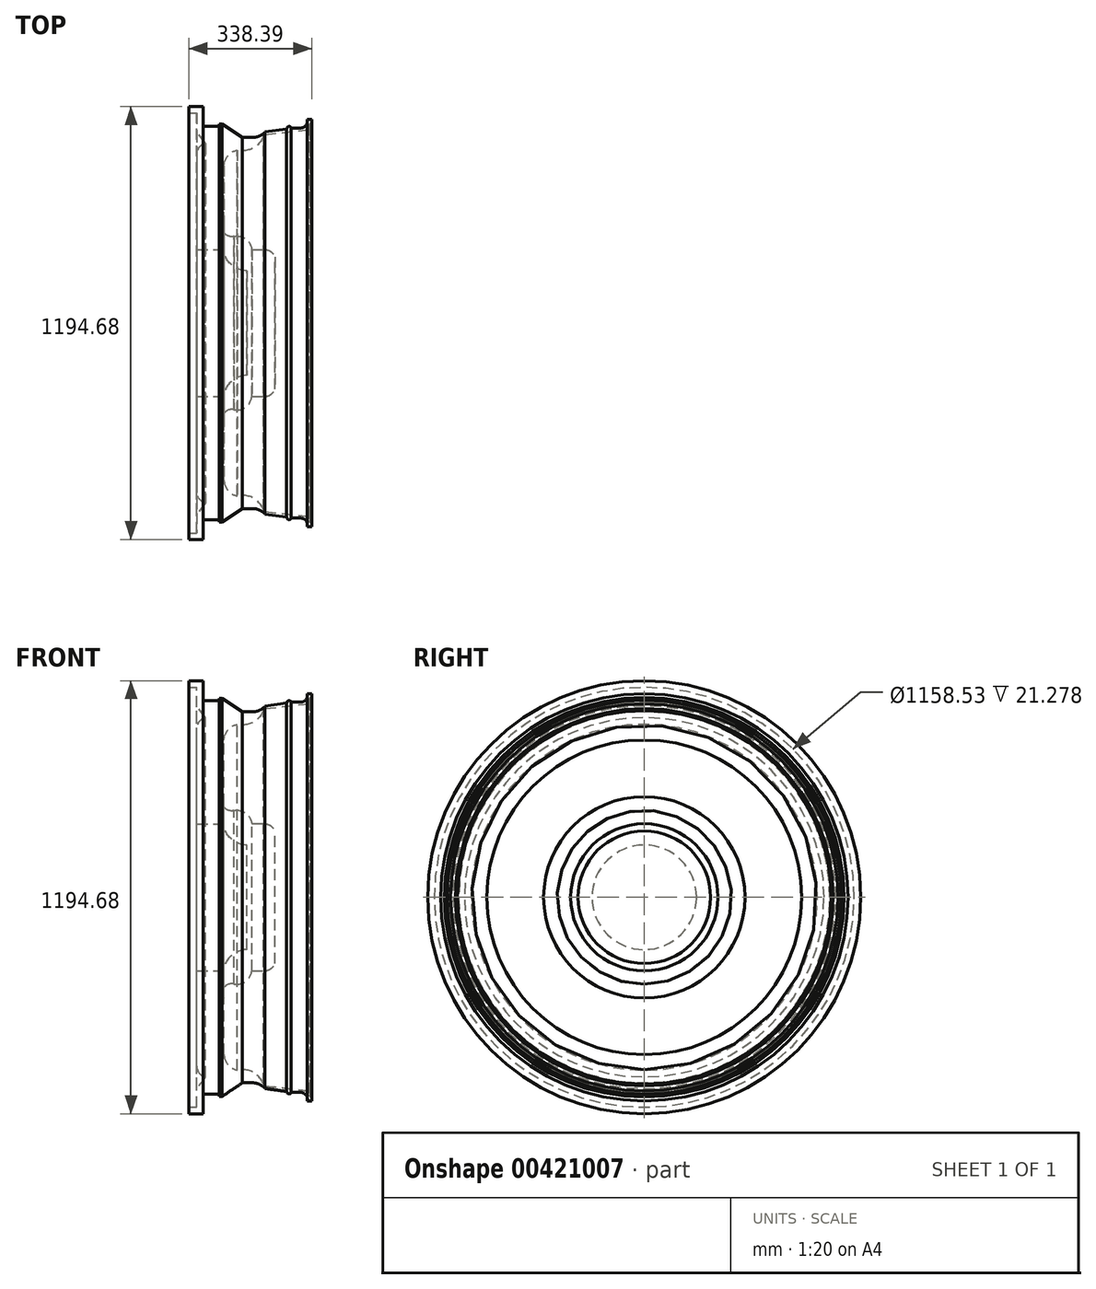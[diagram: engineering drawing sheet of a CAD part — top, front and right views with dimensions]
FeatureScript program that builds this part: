
annotation { "Feature Type Name" : "Feature", "Feature Type Description" : "" }
export const myFeature = defineFeature(function(context is Context, id is Id, definition is map)
    precondition{}
    {
        {
            var Q0;
            Q0=qCreatedBy(makeId("Front.planeOp"),FACE);
            var sketch = newSketch(context, id + "F0", { "sketchPlane" : qUnion([Q0])});
            skLineSegment(sketch, "E0", {"start": v(0, 0) * mm, "end": v(0, 51.45) * mm});
            skLineSegment(sketch, "E1", {"start": v(0, 51.45) * mm, "end": v(-21.28, 51.45) * mm});
            skLineSegment(sketch, "E2", {"start": v(-21.28, 51.45) * mm, "end": v(-21.28, 69.52) * mm});
            skLineSegment(sketch, "E3", {"start": v(-21.28, 69.52) * mm, "end": v(17.49, 69.52) * mm});
            skLineSegment(sketch, "E4", {"start": v(17.49, 69.52) * mm, "end": v(17.49, 15.3) * mm});
            skLineSegment(sketch, "E5", {"start": v(17.49, 15.3) * mm, "end": v(62.67, 15.3) * mm});
            skLineSegment(sketch, "E6", {"start": v(62.67, 15.3) * mm, "end": v(62.67, 21.71) * mm});
            skLineSegment(sketch, "E7", {"start": v(62.67, 21.71) * mm, "end": v(69.66, 21.71) * mm});
            skLineSegment(sketch, "E8", {"start": v(69.66, 21.71) * mm, "end": v(125.92, -15.89) * mm});
            skLineSegment(sketch, "E9", {"start": v(125.92, -15.89) * mm, "end": v(153.9, -15.89) * mm});
            skPoint(sketch, "E10.second.point", {"position": v(166.86, 24.98) * mm});
            skPoint(sketch, "E10.third.point", {"position": v(171.02, 20.3) * mm});
            skArc(sketch, "E11", {"start": v(153.9, -15.89) * mm, "mid": v(172.93, -11.72) * mm, "end": v(188.48, 0) * mm});
            skLineSegment(sketch, "E12", {"start": v(188.48, 0) * mm, "end": v(248.12, 8.07) * mm});
            skArc(sketch, "E13", {"start": v(260.87, 10.5) * mm, "mid": v(253.5, 14.51) * mm, "end": v(248.12, 8.07) * mm});
            skLineSegment(sketch, "E14", {"start": v(260.87, 10.5) * mm, "end": v(286.43, 10.5) * mm});
            skArc(sketch, "E15", {"start": v(286.43, 10.5) * mm, "mid": v(301.45, 17.77) * mm, "end": v(305.08, 34.05) * mm});
            skLineSegment(sketch, "E16", {"start": v(305.08, 34.05) * mm, "end": v(317.1, 34.05) * mm});
            skLineSegment(sketch, "E17", {"start": v(317.1, 34.05) * mm, "end": v(317.1, 23.36) * mm});
            skArc(sketch, "E18", {"start": v(317.1, 23.36) * mm, "mid": v(311.85, 21.3) * mm, "end": v(313.1, 15.79) * mm});
            skLineSegment(sketch, "E19", {"start": v(313.1, 15.79) * mm, "end": v(313.1, 6.43) * mm});
            skLineSegment(sketch, "E20", {"start": v(313.1, 6.43) * mm, "end": v(188.48, -7.27) * mm});
            skLineSegment(sketch, "E21", {"start": v(188.48, -7.27) * mm, "end": v(189.1, -11.9) * mm});
            skLineSegment(sketch, "E22", {"start": v(189.1, -11.9) * mm, "end": v(183.86, -12.61) * mm});
            skArc(sketch, "E23", {"start": v(111.37, -50.63) * mm, "mid": v(154.8, -45.33) * mm, "end": v(183.86, -12.61) * mm});
            skArc(sketch, "E24", {"start": v(111.37, -50.63) * mm, "mid": v(85.88, -66.08) * mm, "end": v(74.86, -93.79) * mm});
            skLineSegment(sketch, "E25", {"start": v(74.86, -93.79) * mm, "end": v(74.86, -250.05) * mm});
            skArc(sketch, "E26", {"start": v(74.86, -250.05) * mm, "mid": v(75.67, -279.11) * mm, "end": v(103.2, -288.47) * mm});
            skArc(sketch, "E27", {"start": v(151.74, -324.87) * mm, "mid": v(135.52, -295.94) * mm, "end": v(103.2, -288.47) * mm});
            skLineSegment(sketch, "E28", {"start": v(151.74, -324.87) * mm, "end": v(186.11, -324.87) * mm});
            skArc(sketch, "E29", {"start": v(215.43, -345.09) * mm, "mid": v(203.92, -330.41) * mm, "end": v(186.11, -324.87) * mm});
            skLineSegment(sketch, "E30", {"start": v(215.43, -345.09) * mm, "end": v(215.43, -527.82) * mm});
            skLineSegment(sketch, "E31", {"start": v(215.43, -527.82) * mm, "end": v(138.13, -527.82) * mm});
            skLineSegment(sketch, "E32", {"start": v(138.13, -527.82) * mm, "end": v(138.13, -383.57) * mm});
            skArc(sketch, "E33", {"start": v(73.52, -324.97) * mm, "mid": v(94.81, -366.41) * mm, "end": v(138.13, -383.57) * mm});
            skLineSegment(sketch, "E34", {"start": v(73.52, -324.97) * mm, "end": v(0, -324.97) * mm});
            skLineSegment(sketch, "E35", {"start": v(0, -324.97) * mm, "end": v(0, -62.03) * mm});
            skArc(sketch, "E36", {"start": v(23.93, -31.98) * mm, "mid": v(6.71, -42.82) * mm, "end": v(0, -62.03) * mm});
            skLineSegment(sketch, "E37", {"start": v(23.93, -31.98) * mm, "end": v(0, 0) * mm});
            skSolve(sketch);
        }
        {
            var Q0;
            Q0=makeQuery(id+"F0.imprint","IMPRINT",FACE,{"disambiguationData":[TD([[makeQuery(id+"F0.imprint","IMPRINT",EDGE,{"derivedFrom":sQuery(id+"F0.wireOp",EDGE,"E0")}),-1.0]])]});
            var Q1;
            Q1=sQuery(id+"F0.wireOp",EDGE,"E31");
            revolve(context, id + "F1", {"entities" : qUnion([Q0]), "axis" : qUnion([Q1]), "revolveType" : RevolveType.FULL});
        }
    });
